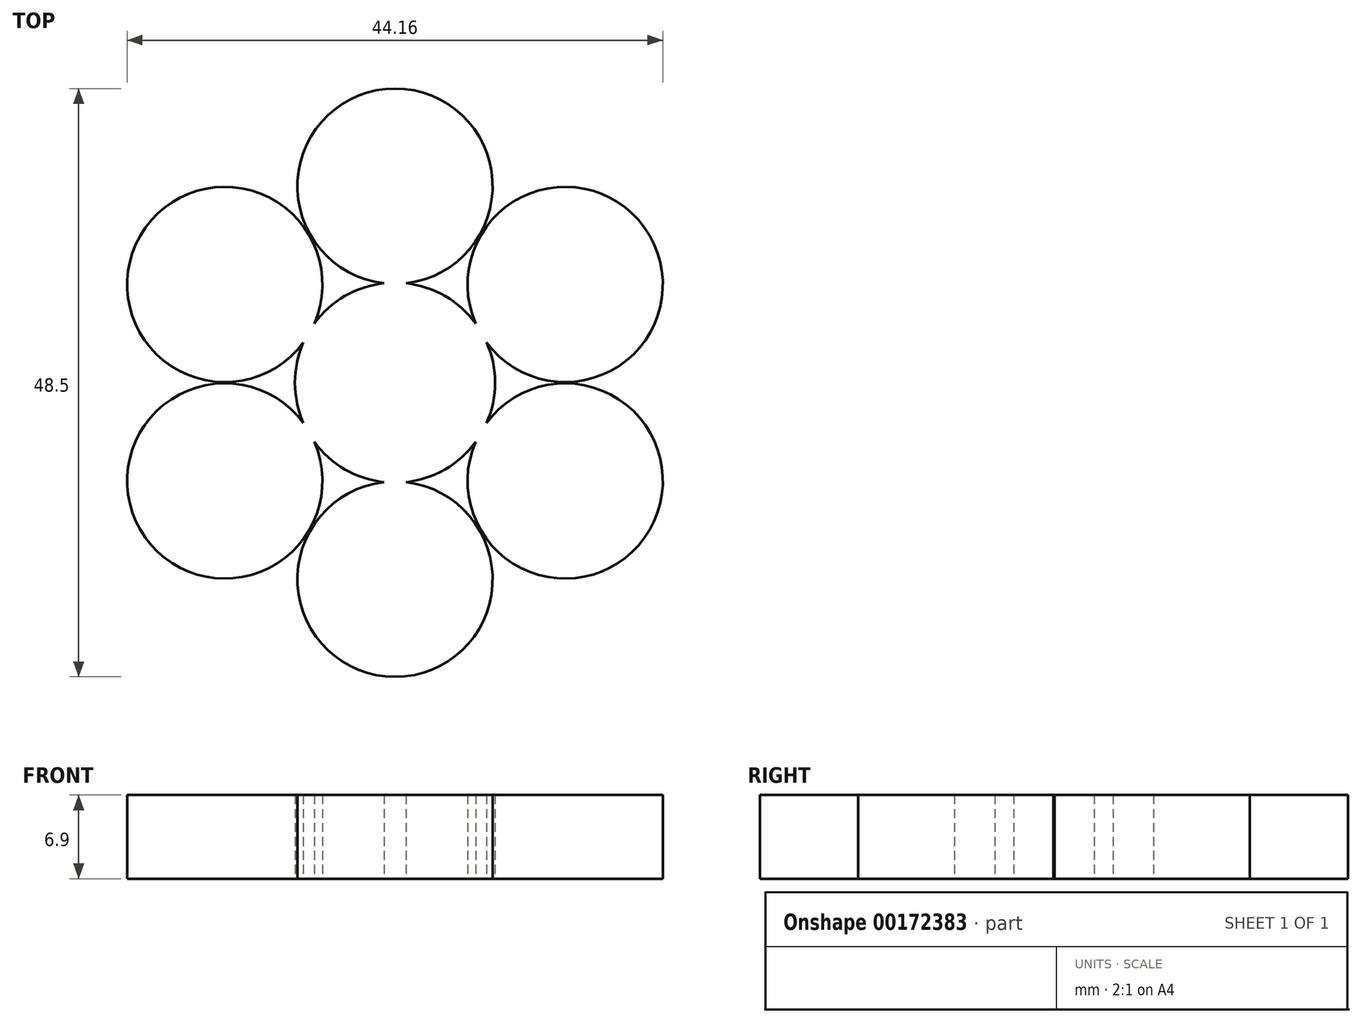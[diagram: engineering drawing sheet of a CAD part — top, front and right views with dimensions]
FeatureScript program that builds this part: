
annotation { "Feature Type Name" : "Feature", "Feature Type Description" : "" }
export const myFeature = defineFeature(function(context is Context, id is Id, definition is map)
    precondition{}
    {
        {
            var Q0;
            Q0=qCreatedBy(makeId("Top.planeOp"),FACE);
            var sketch = newSketch(context, id + "F0", { "sketchPlane" : qUnion([Q0])});
            skArc(sketch, "E0", {"start": v(-31.54, -5.15) * mm, "mid": v(-32.44, 10.9) * mm, "end": v(-33.34, -5.15) * mm});
            skCircle(sketch, "E1", {"center": v(-32.44, -13.35) * mm, "radius": 24.25 * mm, "construction": true});
            skArc(sketch, "E2.1.0", {"start": v(-39.09, -8.47) * mm, "mid": v(-53.44, -1.23) * mm, "end": v(-39.99, -10.03) * mm});
            skArc(sketch, "E2.2.0", {"start": v(-39.99, -16.67) * mm, "mid": v(-53.44, -25.48) * mm, "end": v(-39.09, -18.23) * mm});
            skArc(sketch, "E2.3.0", {"start": v(-33.34, -21.55) * mm, "mid": v(-32.44, -37.6) * mm, "end": v(-31.54, -21.55) * mm});
            skArc(sketch, "E2.4.0", {"start": v(-25.79, -18.23) * mm, "mid": v(-11.44, -25.48) * mm, "end": v(-24.88, -16.67) * mm});
            skArc(sketch, "E3", {"start": v(-39.99, -10.03) * mm, "mid": v(-40.69, -13.35) * mm, "end": v(-39.99, -16.67) * mm});
            skArc(sketch, "E4.1.5.0", {"start": v(-24.88, -10.03) * mm, "mid": v(-11.44, -1.23) * mm, "end": v(-25.79, -8.47) * mm});
            skArc(sketch, "E5.trimOffspring", {"start": v(-39.09, -18.23) * mm, "mid": v(-36.56, -20.5) * mm, "end": v(-33.34, -21.55) * mm});
            skArc(sketch, "E6.trimOffspring", {"start": v(-33.34, -5.15) * mm, "mid": v(-36.56, -6.2) * mm, "end": v(-39.09, -8.47) * mm});
            skArc(sketch, "E7.trimOffspring", {"start": v(-25.79, -8.47) * mm, "mid": v(-28.31, -6.2) * mm, "end": v(-31.54, -5.15) * mm});
            skArc(sketch, "E8.trimOffspring", {"start": v(-24.88, -16.67) * mm, "mid": v(-24.19, -13.35) * mm, "end": v(-24.88, -10.03) * mm});
            skArc(sketch, "E9.trimOffspring", {"start": v(-31.54, -21.55) * mm, "mid": v(-28.31, -20.5) * mm, "end": v(-25.79, -18.23) * mm});
            skSolve(sketch);
        }
        {
            var Q0;
            Q0 = qSketchRegion(id + "F0", true);
            extrude(context, id + "F1", {"entities" : qUnion([Q0]), "depth" : 6.9 * mm});
        }
    });
